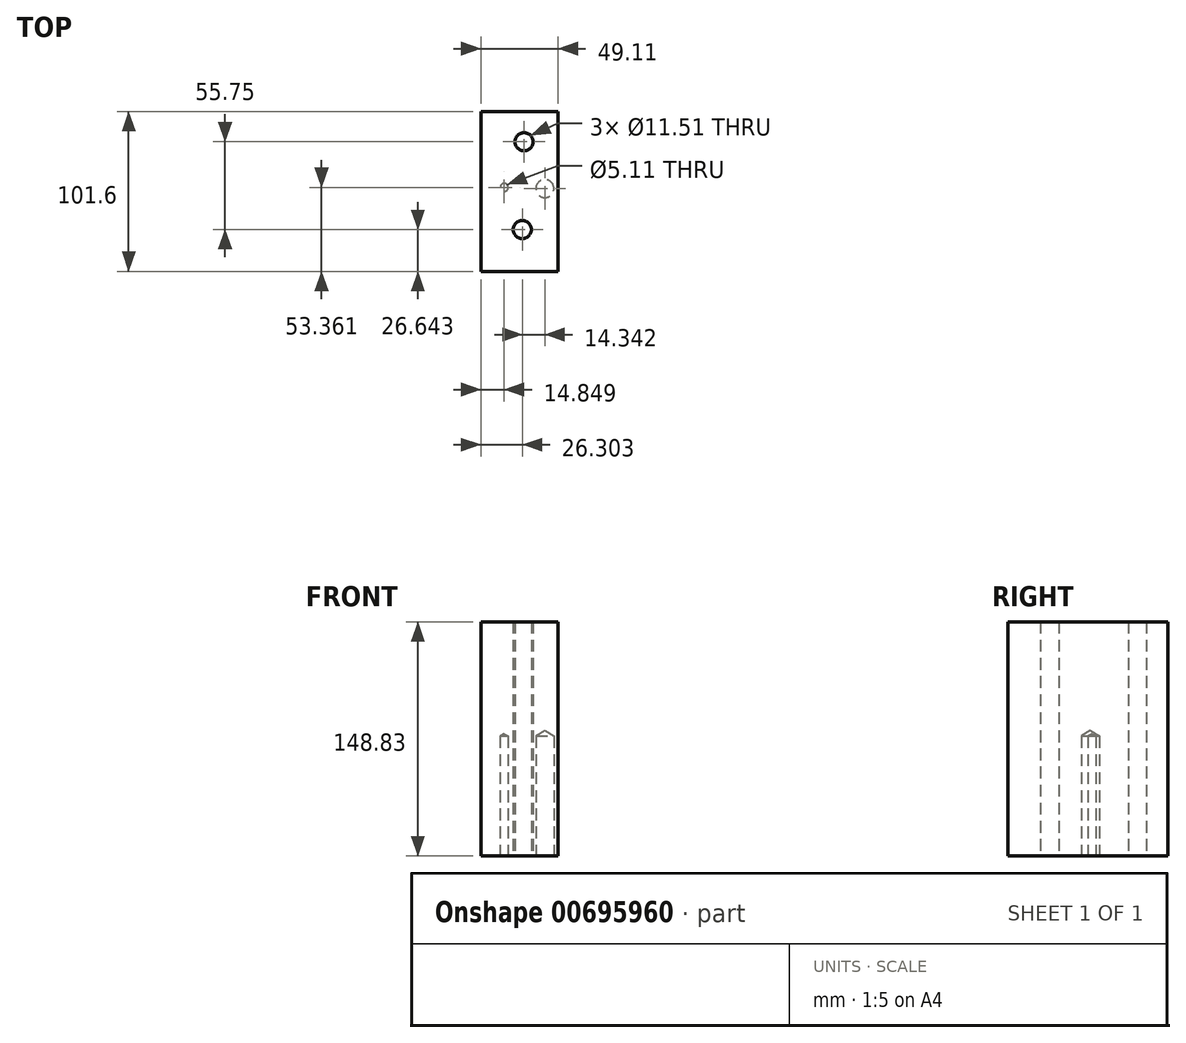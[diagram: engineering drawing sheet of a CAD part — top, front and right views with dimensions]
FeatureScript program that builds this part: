
annotation { "Feature Type Name" : "Feature", "Feature Type Description" : "" }
export const myFeature = defineFeature(function(context is Context, id is Id, definition is map)
    precondition{}
    {
        {
            var Q0;
            Q0=qCreatedBy(makeId("Front.planeOp"),FACE);
            var sketch = newSketch(context, id + "F0", { "sketchPlane" : qUnion([Q0])});
            skLineSegment(sketch, "E0.bottom", {"start": v(-6.4, 39.8) * mm, "end": v(93.5, 39.8) * mm});
            skLineSegment(sketch, "E0.top", {"start": v(-6.4, -7.43) * mm, "end": v(93.5, -7.43) * mm});
            skLineSegment(sketch, "E0.left", {"start": v(-6.4, 39.8) * mm, "end": v(-6.4, -7.43) * mm});
            skLineSegment(sketch, "E0.right", {"start": v(93.5, 39.8) * mm, "end": v(93.5, -7.43) * mm});
            skSolve(sketch);
        }
        {
            var Q0;
            Q0 = qSketchRegion(id + "F0", true);
            extrude(context, id + "F1", {"entities" : qUnion([Q0]), "depth" : 152.4 * mm, "offsetDistance" : 25.4 * mm});
        }
        {
            var Q0;
            Q0=makeQuery(id+"F1.opExtrude","SWEPT_FACE",FACE,{"disambiguationData":[OSD([sQuery(id+"F0.wireOp",EDGE,"E0.bottom")])]});
            extrude(context, id + "F2", {"entities" : qUnion([Q0]), "operationType" : NewBodyOperationType.ADD, "depth" : 50.8 * mm, "offsetDistance" : 25.4 * mm});
        }
        {
            var Q0;
            Q0=makeQuery(id+"F2.opExtrude","CAP_FACE",FACE,{"disambiguationData":[OSD([sQuery(id+"F0.wireOp",EDGE,"E0.bottom")])],"isStart":false});
            extrude(context, id + "F3", {"entities" : qUnion([Q0]), "operationType" : NewBodyOperationType.ADD, "depth" : 50.8 * mm, "offsetDistance" : 25.4 * mm});
        }
        {
            var Q0;
            {var subQ0=sQuery(id+"F0.wireOp",EDGE,"E0.left");var subQ1=sQuery(id+"F0.wireOp",EDGE,"E0.bottom");Q0=makeQuery(id+"F3.boolean.opBoolean","MERGE",FACE,{"derivedFrom":[makeQuery(id+"F2.boolean.opBoolean","MERGE",FACE,{"derivedFrom":[makeQuery(id+"F1.opExtrude","SWEPT_FACE",FACE,{"disambiguationData":[OSD([subQ0])]}),makeQuery(id+"F2.opExtrude","SWEPT_FACE",FACE,{"disambiguationData":[OSD([subQ1,subQ0])]})]}),makeQuery(id+"F3.opExtrude","SWEPT_FACE",FACE,{"disambiguationData":[OSD([subQ1,subQ0])]})]});}
            extrude(context, id + "F4", {"entities" : qUnion([Q0]), "operationType" : NewBodyOperationType.REMOVE, "oppositeDirection" : true, "depth" : 50.8 * mm, "offsetDistance" : 25.4 * mm});
        }
        {
            var Q0;
            {var subQ0=sQuery(id+"F0.wireOp",EDGE,"E0.bottom");var subQ1=makeQuery(id+"F1.opExtrude","CAP_EDGE",EDGE,{"disambiguationData":[OSD([subQ0])],"isStart":true});Q0=makeQuery(id+"F3.boolean.opBoolean","MERGE",FACE,{"derivedFrom":[makeQuery(id+"F2.boolean.opBoolean","MERGE",FACE,{"derivedFrom":[makeQuery(id+"F1.opExtrude","CAP_FACE",FACE,{"disambiguationData":[OSD([subQ0,sQuery(id+"F0.wireOp",EDGE,"E0.top"),sQuery(id+"F0.wireOp",EDGE,"E0.left"),sQuery(id+"F0.wireOp",EDGE,"E0.right")])],"isStart":true}),makeQuery(id+"F2.opExtrude","SWEPT_FACE",FACE,{"disambiguationData":[OSD([subQ0]),TDD([subQ1])]})]}),makeQuery(id+"F3.opExtrude","SWEPT_FACE",FACE,{"disambiguationData":[OSD([subQ0]),TDD([makeQuery(id+"F2.opExtrude","CAP_EDGE",EDGE,{"disambiguationData":[OSD([subQ0]),TDD([subQ1])],"isStart":false})])]})]});}
            extrude(context, id + "F5", {"entities" : qUnion([Q0]), "operationType" : NewBodyOperationType.REMOVE, "oppositeDirection" : true, "depth" : 50.8 * mm, "offsetDistance" : 25.4 * mm});
        }
        {
            var Q0;
            Q0=makeQuery(id+"F1.opExtrude","SWEPT_FACE",FACE,{"disambiguationData":[OSD([sQuery(id+"F0.wireOp",EDGE,"E0.top")])]});
            var sketch = newSketch(context, id + "F6", { "sketchPlane" : qUnion([Q0])});
            skPoint(sketch, "E1", {"position": v(70.7, 125.76) * mm});
            skPoint(sketch, "E2", {"position": v(71.84, 70) * mm});
            skPoint(sketch, "E3", {"position": v(59.41, 98.72) * mm});
            skPoint(sketch, "E4", {"position": v(82.94, 98.34) * mm});
            skSolve(sketch);
        }
        {
            var Q0;
            Q0=sQuery(id+"F6.wireOp",VERTEX,"E1");
            var Q1;
            Q1=sQuery(id+"F6.wireOp",VERTEX,"E2");
            var Q2;
            Q2=makeQuery(id+"F1.opExtrude","SWEPT_BODY",BODY,{"disambiguationData":[OSD([sQuery(id+"F0.wireOp",EDGE,"E0.bottom"),sQuery(id+"F0.wireOp",EDGE,"E0.top"),sQuery(id+"F0.wireOp",EDGE,"E0.left"),sQuery(id+"F0.wireOp",EDGE,"E0.right")])]});
            hole(context, id + "F7", {"style" : HoleStyle.SIMPLE, "endStyle" : HoleEndStyle.THROUGH, "standardTappedOrClearance" : lookupTablePath({ "standard" : "ANSI", "engagement" : "75%", "pitch" : "20 tpi", "size" : "1/2", "type" : "Tapped" }), "standardBlindInLast" : lookupTablePath({ "standard" : "ANSI", "engagement" : "75%", "pitch" : "20 tpi", "size" : "1/2", "type" : "Tapped" }), "holeDiameter" : 11.5 * mm, "majorDiameter" : 12.7 * mm, "showTappedDepth" : true, "tappedDepth" : 12.7 * mm, "tapClearance" : 3, "locations" : qUnion([Q0, Q1]), "scope" : qUnion([Q2])});
        }
        {
            var Q0;
            Q0=makeQuery(id+"F1.opExtrude","SWEPT_FACE",FACE,{"disambiguationData":[OSD([sQuery(id+"F0.wireOp",EDGE,"E0.top")])]});
            var sketch = newSketch(context, id + "F8", { "sketchPlane" : qUnion([Q0])});
            skPoint(sketch, "E5", {"position": v(85.04, 99.8) * mm});
            skSolve(sketch);
        }
        {
            var Q0;
            {var subQ0=sQuery(id+"F0.wireOp",EDGE,"E0.top");Q0=makeQuery(id+"F8.imprint","IMPRINT",FACE,{"disambiguationData":[TD([[makeQuery(id+"F8.imprint","IMPRINT",EDGE,{"derivedFrom":makeQuery(id+"F1.opExtrude","CAP_EDGE",EDGE,{"disambiguationData":[OSD([subQ0])],"isStart":false})}),-1.0]])]});}
            var sketch = newSketch(context, id + "F9", { "sketchPlane" : qUnion([Q0])});
            skPoint(sketch, "E6", {"position": v(59.25, 99.04) * mm});
            skSolve(sketch);
        }
        {
            var Q0;
            Q0=sQuery(id+"F8.wireOp",VERTEX,"E5");
            var Q1;
            Q1=makeQuery(id+"F1.opExtrude","SWEPT_BODY",BODY,{"disambiguationData":[OSD([sQuery(id+"F0.wireOp",EDGE,"E0.bottom"),sQuery(id+"F0.wireOp",EDGE,"E0.top"),sQuery(id+"F0.wireOp",EDGE,"E0.left"),sQuery(id+"F0.wireOp",EDGE,"E0.right")])]});
            hole(context, id + "F10", {"style" : HoleStyle.SIMPLE, "endStyle" : HoleEndStyle.BLIND, "standardTappedOrClearance" : lookupTablePath({ "standard" : "ANSI", "engagement" : "75%", "pitch" : "20 tpi", "size" : "1/2", "type" : "Tapped" }), "standardBlindInLast" : lookupTablePath({ "standard" : "ANSI", "engagement" : "75%", "pitch" : "20 tpi", "size" : "1/2", "type" : "Tapped" }), "holeDiameter" : 11.5 * mm, "majorDiameter" : 12.7 * mm, "showTappedDepth" : true, "holeDepth" : 76.2 * mm, "tappedDepth" : 72.39 * mm, "tapClearance" : 3, "startFromSketch" : true, "locations" : qUnion([Q0]), "scope" : qUnion([Q1])});
        }
        {
            var Q0;
            Q0=sQuery(id+"F9.wireOp",VERTEX,"E6");
            var Q1;
            Q1=makeQuery(id+"F1.opExtrude","SWEPT_BODY",BODY,{"disambiguationData":[OSD([sQuery(id+"F0.wireOp",EDGE,"E0.bottom"),sQuery(id+"F0.wireOp",EDGE,"E0.top"),sQuery(id+"F0.wireOp",EDGE,"E0.left"),sQuery(id+"F0.wireOp",EDGE,"E0.right")])]});
            hole(context, id + "F11", {"style" : HoleStyle.SIMPLE, "endStyle" : HoleEndStyle.BLIND, "standardTappedOrClearance" : lookupTablePath({ "standard" : "ANSI", "engagement" : "75%", "pitch" : "20 tpi", "size" : "1/4", "type" : "Tapped" }), "standardBlindInLast" : lookupTablePath({ "standard" : "ANSI", "engagement" : "75%", "pitch" : "20 tpi", "size" : "1/4", "type" : "Tapped" }), "holeDiameter" : 5.1 * mm, "majorDiameter" : 6.35 * mm, "showTappedDepth" : true, "holeDepth" : 76.2 * mm, "tappedDepth" : 72.39 * mm, "tapClearance" : 3, "startFromSketch" : true, "locations" : qUnion([Q0]), "scope" : qUnion([Q1])});
        }
    });
